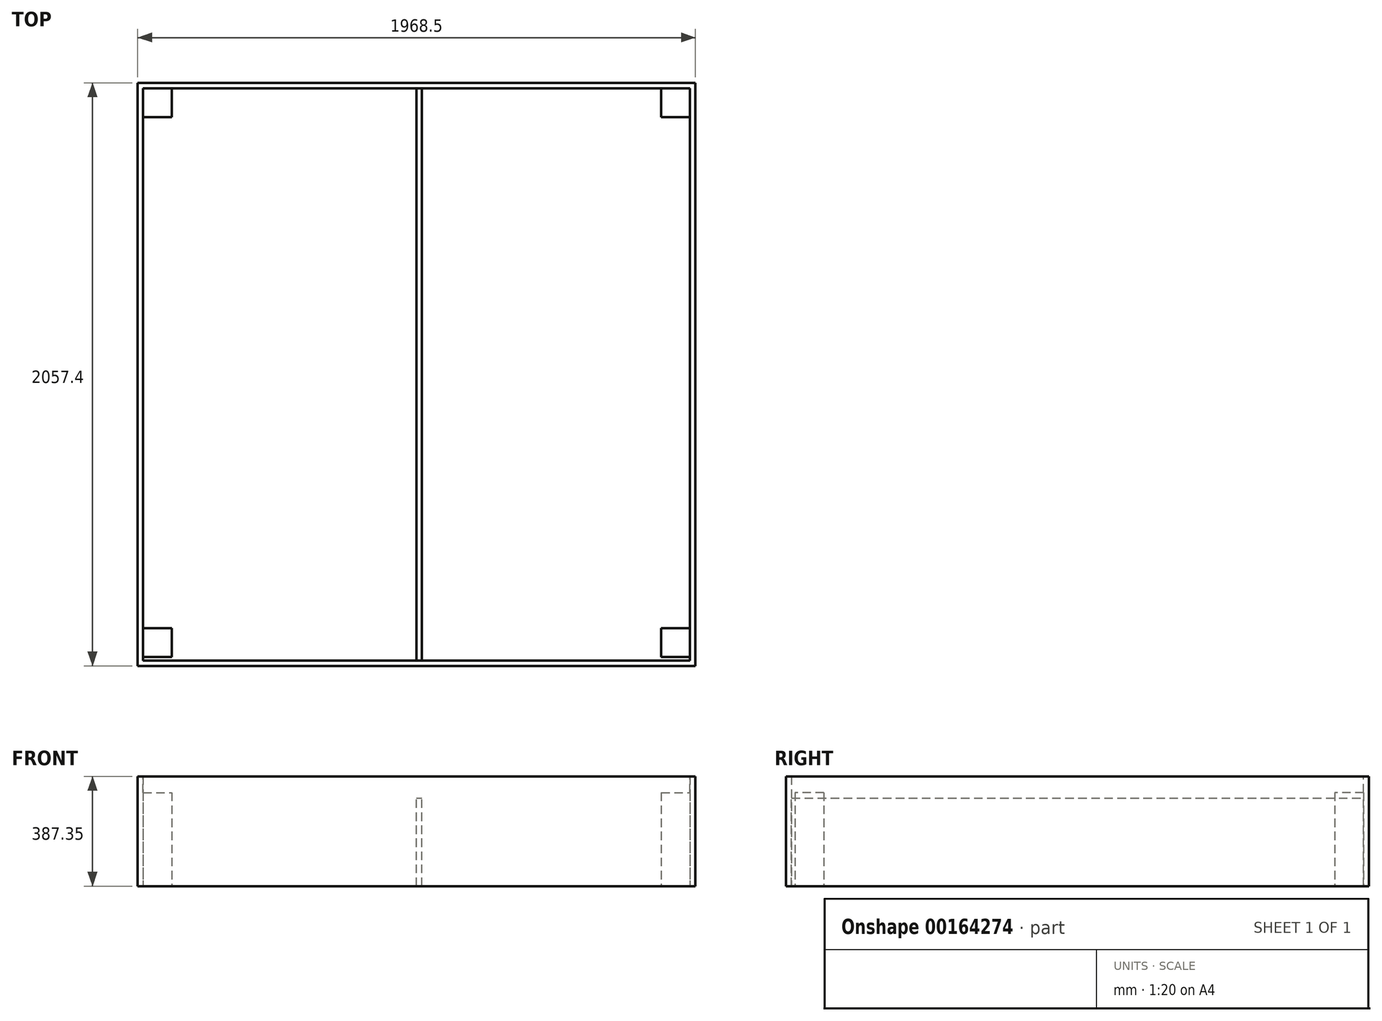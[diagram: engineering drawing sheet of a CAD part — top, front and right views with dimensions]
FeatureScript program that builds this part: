
annotation { "Feature Type Name" : "Feature", "Feature Type Description" : "" }
export const myFeature = defineFeature(function(context is Context, id is Id, definition is map)
    precondition{}
    {
        {
            var Q0;
            Q0=qCreatedBy(makeId("Front.planeOp"),FACE);
            var sketch = newSketch(context, id + "F0", { "sketchPlane" : qUnion([Q0])});
            skLineSegment(sketch, "E0.bottom", {"start": v(0, 0) * mm, "end": v(19.05, 0) * mm});
            skLineSegment(sketch, "E0.top", {"start": v(0, 387.35) * mm, "end": v(19.05, 387.35) * mm});
            skLineSegment(sketch, "E0.left", {"start": v(0, 0) * mm, "end": v(0, 387.35) * mm});
            skLineSegment(sketch, "E0.right", {"start": v(19.05, 0) * mm, "end": v(19.05, 387.35) * mm});
            skSolve(sketch);
        }
        {
            var Q0;
            Q0=makeQuery(id+"F0.imprint","IMPRINT",FACE,{"disambiguationData":[TD([[makeQuery(id+"F0.imprint","IMPRINT",EDGE,{"derivedFrom":sQuery(id+"F0.wireOp",EDGE,"E0.bottom")}),1.0]])]});
            extrude(context, id + "F1", {"entities" : qUnion([Q0]), "depth" : 2057.4 * mm});
        }
        {
            var Q0;
            Q0=makeQuery(id+"F1.opExtrude","SWEPT_FACE",FACE,{"disambiguationData":[OSD([sQuery(id+"F0.wireOp",EDGE,"E0.right")])]});
            var sketch = newSketch(context, id + "F2", { "sketchPlane" : qUnion([Q0])});
            skLineSegment(sketch, "E1.bottom", {"start": v(-2057.4, 387.35) * mm, "end": v(-2038.35, 387.35) * mm});
            skLineSegment(sketch, "E1.top", {"start": v(-2057.4, 0) * mm, "end": v(-2038.35, 0) * mm});
            skLineSegment(sketch, "E1.left", {"start": v(-2057.4, 387.35) * mm, "end": v(-2057.4, 0) * mm});
            skLineSegment(sketch, "E1.right", {"start": v(-2038.35, 387.35) * mm, "end": v(-2038.35, 0) * mm});
            skSolve(sketch);
        }
        {
            var Q0;
            Q0 = qSketchRegion(id + "F2", true);
            extrude(context, id + "F3", {"entities" : qUnion([Q0]), "operationType" : NewBodyOperationType.ADD, "depth" : 1930.4 * mm});
        }
        {
            var Q0;
            Q0=makeQuery(id+"F1.opExtrude","SWEPT_FACE",FACE,{"disambiguationData":[OSD([sQuery(id+"F0.wireOp",EDGE,"E0.right")])]});
            var sketch = newSketch(context, id + "F4", { "sketchPlane" : qUnion([Q0])});
            skLineSegment(sketch, "E2.bottom", {"start": v(0, 0) * mm, "end": v(-19.05, 0) * mm});
            skLineSegment(sketch, "E2.top", {"start": v(0, 387.35) * mm, "end": v(-19.05, 387.35) * mm});
            skLineSegment(sketch, "E2.left", {"start": v(0, 0) * mm, "end": v(0, 387.35) * mm});
            skLineSegment(sketch, "E2.right", {"start": v(-19.05, 0) * mm, "end": v(-19.05, 387.35) * mm});
            skSolve(sketch);
        }
        {
            var Q0;
            Q0 = qSketchRegion(id + "F4", true);
            extrude(context, id + "F5", {"entities" : qUnion([Q0]), "operationType" : NewBodyOperationType.ADD, "depth" : 1930.4 * mm});
        }
        {
            var Q0;
            Q0=qCreatedBy(makeId("Front.planeOp"),FACE);
            var sketch = newSketch(context, id + "F6", { "sketchPlane" : qUnion([Q0])});
            skLineSegment(sketch, "E3.bottom", {"start": v(1949.45, 0) * mm, "end": v(1968.5, 0) * mm});
            skLineSegment(sketch, "E3.top", {"start": v(1949.45, 387.35) * mm, "end": v(1968.5, 387.35) * mm});
            skLineSegment(sketch, "E3.left", {"start": v(1949.45, 0) * mm, "end": v(1949.45, 387.35) * mm});
            skLineSegment(sketch, "E3.right", {"start": v(1968.5, 0) * mm, "end": v(1968.5, 387.35) * mm});
            skSolve(sketch);
        }
        {
            var Q0;
            Q0 = qSketchRegion(id + "F6", true);
            extrude(context, id + "F7", {"entities" : qUnion([Q0]), "operationType" : NewBodyOperationType.ADD, "depth" : 2057.4 * mm});
        }
        {
            var Q0;
            Q0=qCreatedBy(makeId("Top.planeOp"),FACE);
            var sketch = newSketch(context, id + "F8", { "sketchPlane" : qUnion([Q0])});
            skLineSegment(sketch, "E4.bottom", {"start": v(19.05, -19.05) * mm, "end": v(120.65, -19.05) * mm});
            skLineSegment(sketch, "E4.top", {"start": v(19.05, -120.65) * mm, "end": v(120.65, -120.65) * mm});
            skLineSegment(sketch, "E4.left", {"start": v(19.05, -19.05) * mm, "end": v(19.05, -120.65) * mm});
            skLineSegment(sketch, "E4.right", {"start": v(120.65, -19.05) * mm, "end": v(120.65, -120.65) * mm});
            skLineSegment(sketch, "E5.bottom", {"start": v(1847.85, -19.05) * mm, "end": v(1949.45, -19.05) * mm});
            skLineSegment(sketch, "E5.top", {"start": v(1847.85, -120.65) * mm, "end": v(1949.45, -120.65) * mm});
            skLineSegment(sketch, "E5.left", {"start": v(1847.85, -19.05) * mm, "end": v(1847.85, -120.65) * mm});
            skLineSegment(sketch, "E5.right", {"start": v(1949.45, -19.05) * mm, "end": v(1949.45, -120.65) * mm});
            skLineSegment(sketch, "E6.bottom", {"start": v(19.05, -1924.05) * mm, "end": v(120.65, -1924.05) * mm});
            skLineSegment(sketch, "E6.top", {"start": v(19.05, -2025.65) * mm, "end": v(120.65, -2025.65) * mm});
            skLineSegment(sketch, "E6.left", {"start": v(19.05, -1924.05) * mm, "end": v(19.05, -2025.65) * mm});
            skLineSegment(sketch, "E6.right", {"start": v(120.65, -1924.05) * mm, "end": v(120.65, -2025.65) * mm});
            skLineSegment(sketch, "E7.bottom", {"start": v(1847.85, -1924.05) * mm, "end": v(1949.45, -1924.05) * mm});
            skLineSegment(sketch, "E7.top", {"start": v(1847.85, -2025.65) * mm, "end": v(1949.45, -2025.65) * mm});
            skLineSegment(sketch, "E7.left", {"start": v(1847.85, -1924.05) * mm, "end": v(1847.85, -2025.65) * mm});
            skLineSegment(sketch, "E7.right", {"start": v(1949.45, -1924.05) * mm, "end": v(1949.45, -2025.65) * mm});
            skSolve(sketch);
        }
        {
            var Q0;
            Q0=makeQuery(id+"F8.imprint","IMPRINT",FACE,{"disambiguationData":[TD([[makeQuery(id+"F8.imprint","IMPRINT",EDGE,{"derivedFrom":sQuery(id+"F8.wireOp",EDGE,"E4.bottom")}),-1.0]])]});
            var Q1;
            Q1=makeQuery(id+"F8.imprint","IMPRINT",FACE,{"disambiguationData":[TD([[makeQuery(id+"F8.imprint","IMPRINT",EDGE,{"derivedFrom":sQuery(id+"F8.wireOp",EDGE,"E5.bottom")}),-1.0]])]});
            var Q2;
            Q2=makeQuery(id+"F8.imprint","IMPRINT",FACE,{"disambiguationData":[TD([[makeQuery(id+"F8.imprint","IMPRINT",EDGE,{"derivedFrom":sQuery(id+"F8.wireOp",EDGE,"E7.bottom")}),-1.0]])]});
            var Q3;
            Q3=makeQuery(id+"F8.imprint","IMPRINT",FACE,{"disambiguationData":[TD([[makeQuery(id+"F8.imprint","IMPRINT",EDGE,{"derivedFrom":sQuery(id+"F8.wireOp",EDGE,"E6.bottom")}),-1.0]])]});
            extrude(context, id + "F9", {"entities" : qUnion([Q0, Q1, Q2, Q3]), "operationType" : NewBodyOperationType.ADD, "depth" : 330.2 * mm});
        }
        {
            var Q0;
            Q0=makeQuery(id+"F5.opExtrude","SWEPT_FACE",FACE,{"disambiguationData":[OSD([sQuery(id+"F4.wireOp",EDGE,"E2.right")])]});
            var sketch = newSketch(context, id + "F10", { "sketchPlane" : qUnion([Q0])});
            skLineSegment(sketch, "E8.bottom", {"start": v(984.25, 0) * mm, "end": v(1003.3, 0) * mm});
            skLineSegment(sketch, "E8.top", {"start": v(984.25, 311.15) * mm, "end": v(1003.3, 311.15) * mm});
            skLineSegment(sketch, "E8.left", {"start": v(984.25, 0) * mm, "end": v(984.25, 311.15) * mm});
            skLineSegment(sketch, "E8.right", {"start": v(1003.3, 0) * mm, "end": v(1003.3, 311.15) * mm});
            skSolve(sketch);
        }
        {
            var Q0;
            Q0 = qSketchRegion(id + "F10", true);
            extrude(context, id + "F11", {"entities" : qUnion([Q0]), "operationType" : NewBodyOperationType.ADD, "depth" : 2025.65 * mm});
        }
    });
